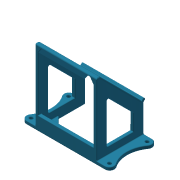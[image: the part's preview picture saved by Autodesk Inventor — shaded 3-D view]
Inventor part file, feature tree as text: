
AUTODESK INVENTOR PART (.ipt)
format: ipt  version: 2014 (Build 180170000, 170)  size: 471,552 bytes
history: native  units: mm
features: fillet x12, extrude x6, sketch x4, chamfer x2
ambient origin geometry x8: Origin, YZ Plane, XZ Plane, XY Plane, X Axis, Y Axis, Z Axis, Center Point
bodies: Solid1 (feature_tree)
feature tree (24):
  extrude  "Extrusion1"  Depth=90.0mm
  extrude  "Extrusion2"  Depth=90.0mm TaperAngle=0.0deg
  extrude  "Extrusion3"  Depth=12.0mm
  extrude  "Extrusion4"  Depth=5.0mm TaperAngle=0.0deg
  extrude  "Extrusion7"  Depth=1.0mm
  chamfer  "Chamfer2"  Distance=4.0mm
  extrude  "Extrusion9"  Depth=80.0mm TaperAngle=0.0deg
  chamfer  "Chamfer4"  Distance=15.0mm
  fillet  "Fillet1"  Radius=15.0mm
  fillet  "Fillet3"  Radius=140.0mm
  fillet  "Fillet4"  Radius=5.0mm
  fillet  "Fillet5"  Radius=2.0mm
  fillet  "Fillet6"  Radius=2.0mm
  fillet  "Fillet7"  Radius=1.0mm
  fillet  "Fillet12"  Radius=1.0mm
  fillet  "Fillet15"  Radius=1.0mm
  fillet  "Fillet16"  Radius=1.0mm
  fillet  "Fillet17"  Radius=1.0mm
  fillet  "Fillet18"  Radius=1.0mm
  fillet  "Fillet19"  Radius=1.0mm
  sketch  "Sketch1"  dims[d0=45.0deg d1=90.0mm]
  sketch  "Sketch3"  dims[d2=45.0mm d3=90.0mm d4=0.0mm]
  sketch  "Sketch7"  dims[d5=4.5mm d6=12.0mm]
  sketch  "Sketch9"  dims[d7=7.0mm d8=5.0mm d9=0.0mm d10=4.0mm d11=4.0mm d12=0.0mm d14=80.0mm d15=0.0mm d26=15.0mm d27=15.0mm d28=15.0mm d29=140.0mm d30=0.0mm d34=5.0mm d35=2.0mm d36=45.0deg d46=2.0mm d48=2.0mm d49=1.0mm d50=1.0mm d51=1.0mm d52=1.0mm d57=1.0mm d60=1.0mm d61=1.0mm d62=108.63961mm d63=5.0mm d64=15.0mm d66=5.0mm d67=40.0mm d68=15.0mm d69=5.0mm d70=20.0mm d71=10.0mm d72=0.0mm d73=10.0mm d74=2.0mm d75=45.0deg d76=1.0mm d77=1.0mm d78=1.0mm d79=12.0mm d80=54.63961mm]
